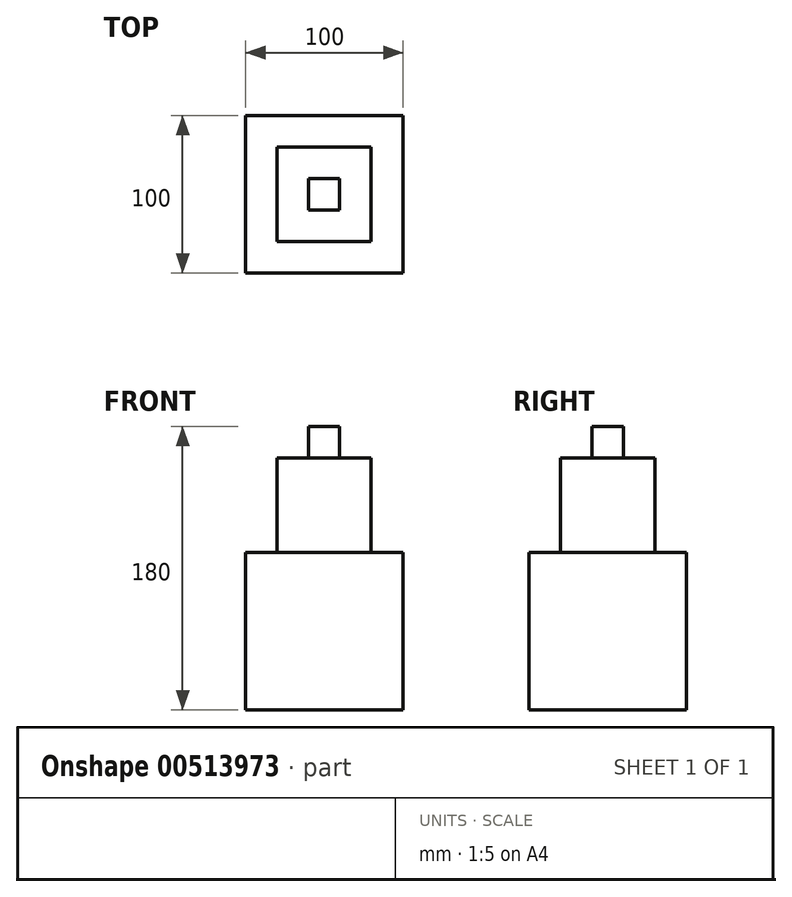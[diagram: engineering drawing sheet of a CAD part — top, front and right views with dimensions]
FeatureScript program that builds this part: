
annotation { "Feature Type Name" : "Feature", "Feature Type Description" : "" }
export const myFeature = defineFeature(function(context is Context, id is Id, definition is map)
    precondition{}
    {
        {
            var Q0;
            Q0=qCreatedBy(makeId("Top.planeOp"),FACE);
            var sketch = newSketch(context, id + "F0", { "sketchPlane" : qUnion([Q0])});
            skLineSegment(sketch, "E0.bottom", {"start": v(-50.16, 54.2) * mm, "end": v(49.84, 54.2) * mm});
            skLineSegment(sketch, "E0.top", {"start": v(-50.16, -45.8) * mm, "end": v(49.84, -45.8) * mm});
            skLineSegment(sketch, "E0.left", {"start": v(-50.16, 54.2) * mm, "end": v(-50.16, -45.8) * mm});
            skLineSegment(sketch, "E0.right", {"start": v(49.84, 54.2) * mm, "end": v(49.84, -45.8) * mm});
            skSolve(sketch);
        }
        {
            var Q0;
            Q0 = qSketchRegion(id + "F0", true);
            extrude(context, id + "F1", {"entities" : qUnion([Q0]), "depth" : 100 * mm, "offsetDistance" : 25 * mm});
        }
        {
            var Q0;
            Q0=makeQuery(id+"F1.opExtrude","CAP_FACE",FACE,{"disambiguationData":[OSD([sQuery(id+"F0.wireOp",EDGE,"E0.bottom"),sQuery(id+"F0.wireOp",EDGE,"E0.top"),sQuery(id+"F0.wireOp",EDGE,"E0.left"),sQuery(id+"F0.wireOp",EDGE,"E0.right")])],"isStart":false});
            var sketch = newSketch(context, id + "F2", { "sketchPlane" : qUnion([Q0])});
            skLineSegment(sketch, "E1.right", {"start": v(49.53, -22.4) * mm, "end": v(49.53, 37.6) * mm});
            skSolve(sketch);
        }
        {
            var Q0;
            Q0=makeQuery(id+"F2.imprint","IMPRINT",FACE,{"disambiguationData":[TD([[makeQuery(id+"F2.imprint","IMPRINT",EDGE,{"derivedFrom":makeQuery(id+"F1.opExtrude","CAP_EDGE",EDGE,{"disambiguationData":[OSD([sQuery(id+"F0.wireOp",EDGE,"E0.bottom")])],"isStart":false})}),-1.0]])]});
            var sketch = newSketch(context, id + "F3", { "sketchPlane" : qUnion([Q0])});
            skLineSegment(sketch, "E2.bottom", {"start": v(-30.16, 34.2) * mm, "end": v(29.53, 34.2) * mm});
            skLineSegment(sketch, "E2.top", {"start": v(-30.16, -25.8) * mm, "end": v(29.53, -25.8) * mm});
            skLineSegment(sketch, "E2.left", {"start": v(-30.16, 34.2) * mm, "end": v(-30.16, -25.8) * mm});
            skLineSegment(sketch, "E2.right", {"start": v(29.53, 34.2) * mm, "end": v(29.53, -25.8) * mm});
            skSolve(sketch);
        }
        {
            var Q0;
            Q0 = qSketchRegion(id + "F3", true);
            extrude(context, id + "F4", {"entities" : qUnion([Q0]), "operationType" : NewBodyOperationType.ADD, "depth" : 60 * mm, "offsetDistance" : 25 * mm});
        }
        {
            var Q0;
            Q0=makeQuery(id+"F4.opExtrude","CAP_FACE",FACE,{"disambiguationData":[OSD([sQuery(id+"F3.wireOp",EDGE,"E2.bottom"),sQuery(id+"F3.wireOp",EDGE,"E2.top"),sQuery(id+"F3.wireOp",EDGE,"E2.left"),sQuery(id+"F3.wireOp",EDGE,"E2.right")])],"isStart":false});
            var sketch = newSketch(context, id + "F5", { "sketchPlane" : qUnion([Q0])});
            skLineSegment(sketch, "E3.bottom", {"start": v(-10.16, 14.2) * mm, "end": v(9.53, 14.2) * mm});
            skLineSegment(sketch, "E3.top", {"start": v(-10.16, -5.8) * mm, "end": v(9.53, -5.8) * mm});
            skLineSegment(sketch, "E3.left", {"start": v(-10.16, 14.2) * mm, "end": v(-10.16, -5.8) * mm});
            skLineSegment(sketch, "E3.right", {"start": v(9.53, 14.2) * mm, "end": v(9.53, -5.8) * mm});
            skSolve(sketch);
        }
        {
            var Q0;
            Q0 = qSketchRegion(id + "F5", true);
            extrude(context, id + "F6", {"entities" : qUnion([Q0]), "operationType" : NewBodyOperationType.ADD, "depth" : 20 * mm, "offsetDistance" : 25 * mm});
        }
    });
